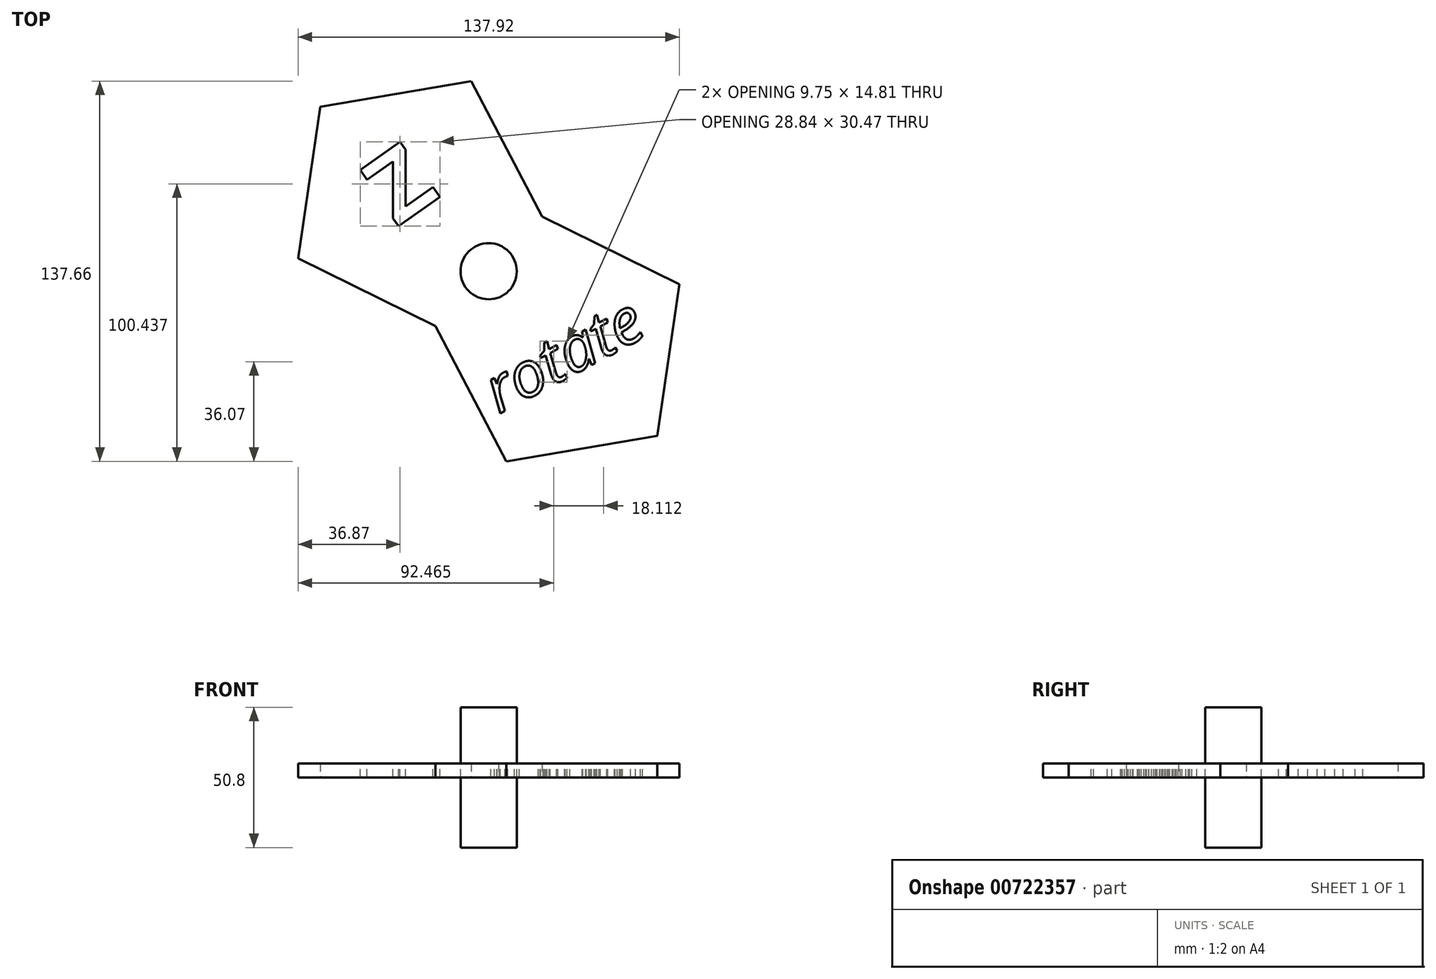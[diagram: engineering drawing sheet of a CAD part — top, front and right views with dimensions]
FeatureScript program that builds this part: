
annotation { "Feature Type Name" : "Feature", "Feature Type Description" : "" }
export const myFeature = defineFeature(function(context is Context, id is Id, definition is map)
    precondition{}
    {
        {
            var Q0;
            Q0=qCreatedBy(makeId("Top.planeOp"),FACE);
            var sketch = newSketch(context, id + "F0", { "sketchPlane" : qUnion([Q0])});
            skCircle(sketch, "E0.cCircle", {"center": v(-27.26, 26.62) * mm, "radius": 38.1 * mm, "construction": true});
            skLineSegment(sketch, "E0.0", {"start": v(19.34, 19.8) * mm, "end": v(-19.34, -19.8) * mm});
            skLineSegment(sketch, "E0.1", {"start": v(-19.34, -19.8) * mm, "end": v(-68.96, 4.74) * mm});
            skLineSegment(sketch, "E0.2", {"start": v(-68.96, 4.74) * mm, "end": v(-60.95, 59.52) * mm});
            skLineSegment(sketch, "E0.3", {"start": v(-60.95, 59.52) * mm, "end": v(-6.38, 68.83) * mm});
            skLineSegment(sketch, "E0.4", {"start": v(-6.38, 68.83) * mm, "end": v(19.34, 19.8) * mm});
            skPoint(sketch, "E0.0.midPoint", {"position": v(0, 0) * mm});
            skSolve(sketch);
        }
        {
            var Q0;
            Q0=qCreatedBy(makeId("Top.planeOp"),FACE);
            var sketch = newSketch(context, id + "F1", { "sketchPlane" : qUnion([Q0])});
            skCircle(sketch, "E1.cCircle", {"center": v(27.26, -26.62) * mm, "radius": 38.1 * mm, "construction": true});
            skLineSegment(sketch, "E1.0", {"start": v(-19.34, -19.8) * mm, "end": v(19.34, 19.8) * mm});
            skLineSegment(sketch, "E1.1", {"start": v(19.34, 19.8) * mm, "end": v(68.96, -4.74) * mm});
            skLineSegment(sketch, "E1.2", {"start": v(68.96, -4.74) * mm, "end": v(60.95, -59.52) * mm});
            skLineSegment(sketch, "E1.3", {"start": v(60.95, -59.52) * mm, "end": v(6.38, -68.83) * mm});
            skLineSegment(sketch, "E1.4", {"start": v(6.38, -68.83) * mm, "end": v(-19.34, -19.8) * mm});
            skPoint(sketch, "E1.0.midPoint", {"position": v(0, 0) * mm});
            skSolve(sketch);
        }
        {
            var Q0;
            Q0=makeQuery(id+"F1.imprint","IMPRINT",FACE,{"disambiguationData":[TD([[makeQuery(id+"F1.imprint","IMPRINT",EDGE,{"derivedFrom":sQuery(id+"F1.wireOp",EDGE,"E1.0")}),-1.0]])]});
            extrude(context, id + "F2", {"entities" : qUnion([Q0]), "depth" : 5.08 * mm, "offsetDistance" : 25.4 * mm});
        }
        {
            var Q0;
            Q0 = qSketchRegion(id + "F0", true);
            extrude(context, id + "F3", {"entities" : qUnion([Q0]), "operationType" : NewBodyOperationType.ADD, "depth" : 5.08 * mm, "offsetDistance" : 25.4 * mm});
        }
        {
            var Q0;
            Q0=qCreatedBy(makeId("Top.planeOp"),FACE);
            var sketch = newSketch(context, id + "F4", { "sketchPlane" : qUnion([Q0])});
            skCircle(sketch, "E2", {"center": v(0, 0) * mm, "radius": 10.16 * mm});
            skSolve(sketch);
        }
        {
            var Q0;
            Q0 = qSketchRegion(id + "F4", true);
            extrude(context, id + "F5", {"entities" : qUnion([Q0]), "oppositeDirection" : true, "depth" : 25.4 * mm, "offsetDistance" : 25.4 * mm, "hasSecondDirection" : true, "secondDirectionOppositeDirection" : false, "secondDirectionDepth" : 25.4 * mm});
        }
        {
            var Q0;
            Q0=qCreatedBy(makeId("Top.planeOp"),FACE);
            var sketch = newSketch(context, id + "F6", { "sketchPlane" : qUnion([Q0])});
            skText(sketch, "E3", { "text": "Z", "fontName": "OpenSans-Bold.ttf"});
            const initialGuessF6  = {"E3": [-0.03334, 0.0159, 0.81915, 0.57358, 0.02481]};
            skSetInitialGuess(sketch, initialGuessF6);
            skSolve(sketch);
        }
        {
            var Q0;
            Q0 = qSketchRegion(id + "F6", true);
            extrude(context, id + "F7", {"entities" : qUnion([Q0]), "operationType" : NewBodyOperationType.REMOVE, "oppositeDirection" : true, "depth" : 5.08 * mm, "offsetDistance" : 25.4 * mm, "hasSecondDirection" : true, "secondDirectionOppositeDirection" : false, "secondDirectionDepth" : 25.4 * mm});
        }
        {
            var Q0;
            Q0=qCreatedBy(makeId("Top.planeOp"),FACE);
            var sketch = newSketch(context, id + "F8", { "sketchPlane" : qUnion([Q0])});
            skText(sketch, "E4", { "text": "rotate", "fontName": "OpenSans-Italic.ttf"});
            const initialGuessF8  = {"E4": [0.0036, -0.0518, 0.88345, 0.46852, 0.0166]};
            skSetInitialGuess(sketch, initialGuessF8);
            skSolve(sketch);
        }
        {
            var Q0;
            Q0 = qSketchRegion(id + "F8", true);
            extrude(context, id + "F9", {"entities" : qUnion([Q0]), "operationType" : NewBodyOperationType.REMOVE, "oppositeDirection" : true, "depth" : 25.4 * mm, "offsetDistance" : 25.4 * mm});
        }
        {
            var Q0;
            Q0 = qSketchRegion(id + "F8", true);
            extrude(context, id + "F10", {"entities" : qUnion([Q0]), "operationType" : NewBodyOperationType.REMOVE, "oppositeDirection" : true, "depth" : 25.4 * mm, "offsetDistance" : 25.4 * mm, "hasSecondDirection" : true, "secondDirectionOppositeDirection" : false, "secondDirectionDepth" : 25.4 * mm});
        }
    });
